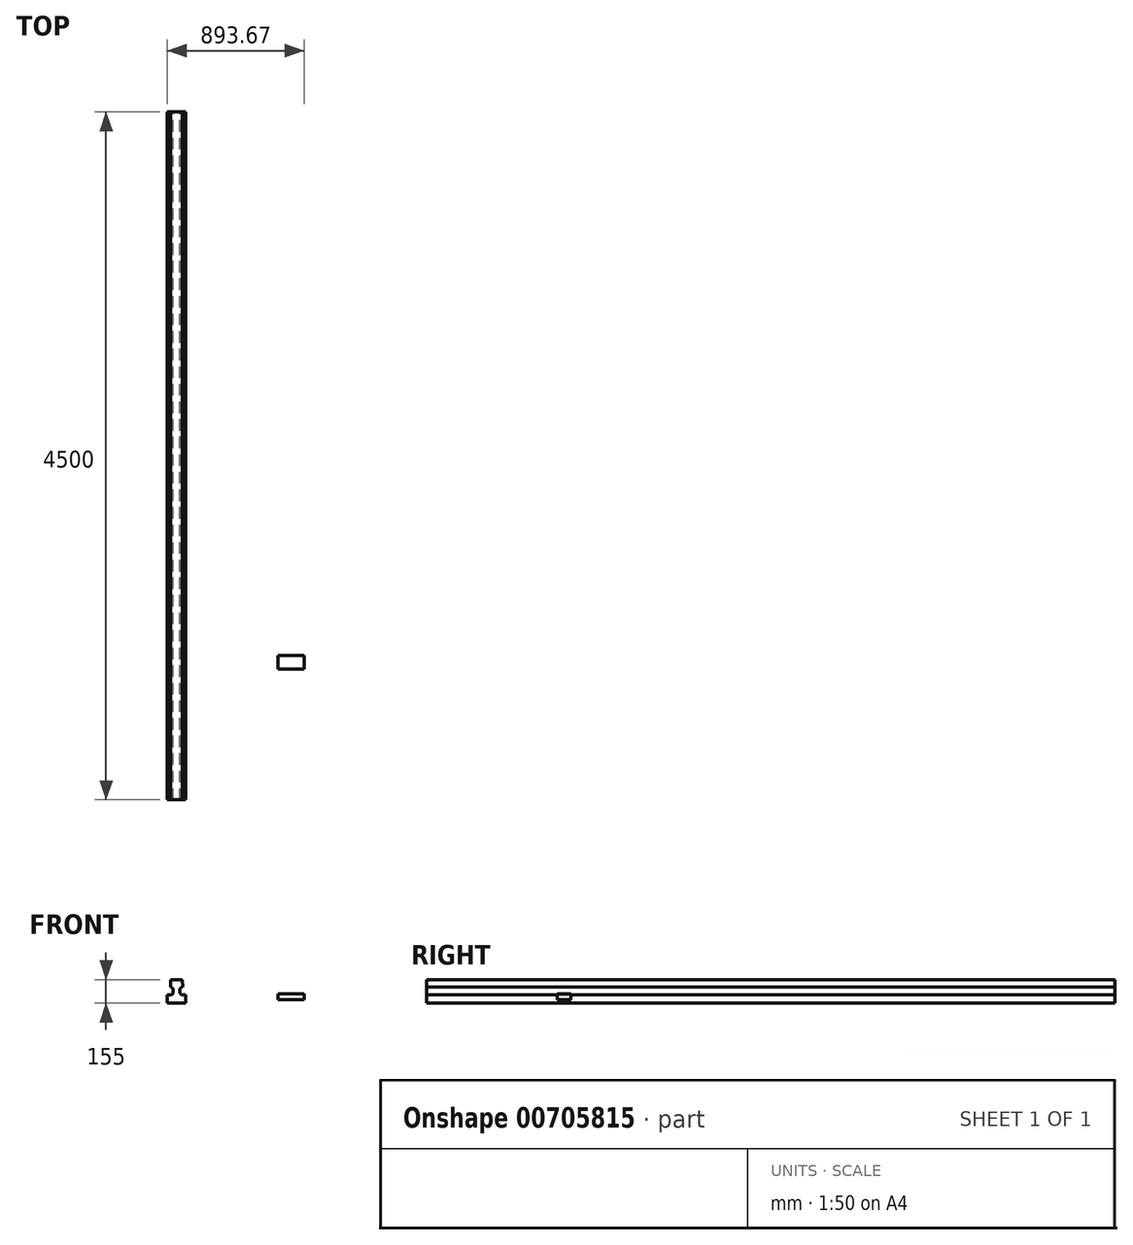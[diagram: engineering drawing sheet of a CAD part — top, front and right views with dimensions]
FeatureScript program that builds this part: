
annotation { "Feature Type Name" : "Feature", "Feature Type Description" : "" }
export const myFeature = defineFeature(function(context is Context, id is Id, definition is map)
    precondition{}
    {
        {
            var Q0;
            Q0=qCreatedBy(makeId("Front.planeOp"),FACE);
            var sketch = newSketch(context, id + "F0", { "sketchPlane" : qUnion([Q0])});
            skLineSegment(sketch, "E0.bottom", {"start": v(-79.3, 132.71) * mm, "end": v(-4.3, 132.71) * mm});
            skLineSegment(sketch, "E0.top", {"start": v(-101.3, -22.29) * mm, "end": v(18.7, -22.29) * mm});
            skLineSegment(sketch, "E0.left", {"start": v(-101.3, 32.71) * mm, "end": v(-101.3, -22.29) * mm});
            skLineSegment(sketch, "E0.right", {"start": v(18.7, 32.71) * mm, "end": v(18.7, -22.29) * mm});
            skLineSegment(sketch, "E1", {"start": v(-101.3, 32.71) * mm, "end": v(-78.8, 32.71) * mm});
            skLineSegment(sketch, "E2", {"start": v(-81.3, 82.71) * mm, "end": v(-78.8, 82.71) * mm});
            skPoint(sketch, "E3", {"position": v(-79.3, 132.71) * mm});
            skPoint(sketch, "E4", {"position": v(-4.3, 132.71) * mm});
            skPoint(sketch, "E5", {"position": v(-81.3, 82.71) * mm});
            skPoint(sketch, "E6", {"position": v(-1.3, 82.71) * mm});
            skLineSegment(sketch, "E7", {"start": v(-79.3, 132.71) * mm, "end": v(-81.3, 82.71) * mm});
            skLineSegment(sketch, "E8", {"start": v(-4.3, 132.71) * mm, "end": v(-1.3, 82.71) * mm});
            skLineSegment(sketch, "E9", {"start": v(-63.8, 67.71) * mm, "end": v(-63.8, 47.71) * mm});
            skLineSegment(sketch, "E10", {"start": v(-18.8, 67.71) * mm, "end": v(-18.8, 47.71) * mm});
            skLineSegment(sketch, "E11", {"start": v(-3.8, 82.71) * mm, "end": v(-1.3, 82.71) * mm});
            skLineSegment(sketch, "E12", {"start": v(-3.8, 32.71) * mm, "end": v(18.7, 32.71) * mm});
            skArc(sketch, "E13.filletArc", {"start": v(-63.8, 67.71) * mm, "mid": v(-68.2, 78.32) * mm, "end": v(-78.8, 82.71) * mm});
            skArc(sketch, "E14.filletArc", {"start": v(-78.8, 32.71) * mm, "mid": v(-68.2, 37.1) * mm, "end": v(-63.8, 47.71) * mm});
            skArc(sketch, "E15.filletArc", {"start": v(-3.8, 82.71) * mm, "mid": v(-14.42, 78.32) * mm, "end": v(-18.8, 67.71) * mm});
            skArc(sketch, "E16.filletArc", {"start": v(-18.8, 47.71) * mm, "mid": v(-14.42, 37.1) * mm, "end": v(-3.8, 32.71) * mm});
            skSolve(sketch);
        }
        {
            var Q0;
            Q0=makeQuery(id+"F0.imprint","IMPRINT",FACE,{"disambiguationData":[TD([[makeQuery(id+"F0.imprint","IMPRINT",EDGE,{"derivedFrom":sQuery(id+"F0.wireOp",EDGE,"E0.bottom")}),-1.0]])]});
            extrude(context, id + "F1", {"entities" : qUnion([Q0]), "depth" : 4500 * mm, "offsetDistance" : 25 * mm});
        }
        {
            var Q0;
            Q0=qCreatedBy(makeId("Top.planeOp"),FACE);
            var sketch = newSketch(context, id + "F2", { "sketchPlane" : qUnion([Q0])});
            skLineSegment(sketch, "E17.bottom", {"start": v(620.36, -3644.7) * mm, "end": v(792.36, -3644.7) * mm});
            skLineSegment(sketch, "E17.top", {"start": v(620.36, -3554.7) * mm, "end": v(792.36, -3554.7) * mm});
            skLineSegment(sketch, "E17.left", {"start": v(620.36, -3644.7) * mm, "end": v(620.36, -3554.7) * mm});
            skLineSegment(sketch, "E17.right", {"start": v(792.36, -3644.7) * mm, "end": v(792.36, -3554.7) * mm});
            skSolve(sketch);
        }
        {
            var Q0;
            Q0=makeQuery(id+"F2.imprint","IMPRINT",FACE,{"disambiguationData":[TD([[makeQuery(id+"F2.imprint","IMPRINT",EDGE,{"derivedFrom":sQuery(id+"F2.wireOp",EDGE,"E17.bottom")}),1.0]])]});
            extrude(context, id + "F3", {"entities" : qUnion([Q0]), "depth" : 40 * mm, "offsetDistance" : 25 * mm});
        }
    });
